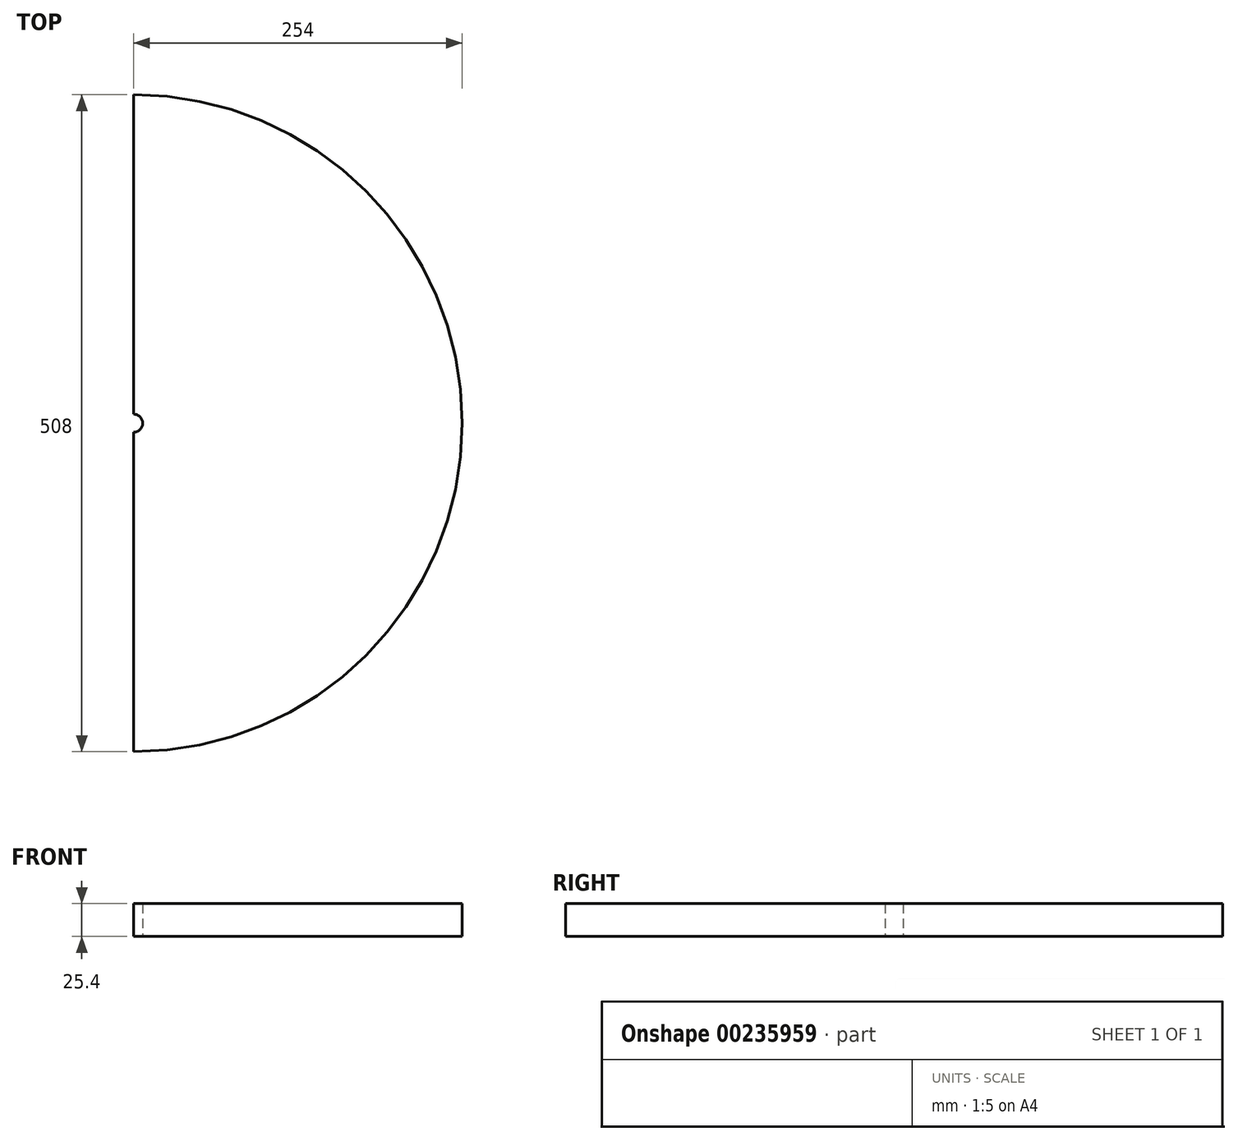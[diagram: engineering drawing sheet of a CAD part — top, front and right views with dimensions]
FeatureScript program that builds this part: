
annotation { "Feature Type Name" : "Feature", "Feature Type Description" : "" }
export const myFeature = defineFeature(function(context is Context, id is Id, definition is map)
    precondition{}
    {
        {
            var Q0;
            Q0=qCreatedBy(makeId("Top.planeOp"),FACE);
            var sketch = newSketch(context, id + "F0", { "sketchPlane" : qUnion([Q0])});
            skCircle(sketch, "E0", {"center": v(0, 0) * mm, "radius": 254 * mm});
            skCircle(sketch, "E1", {"center": v(0, 0) * mm, "radius": 6.99 * mm});
            skLineSegment(sketch, "E2", {"start": v(0, 0) * mm, "end": v(0, 254) * mm});
            skLineSegment(sketch, "E3", {"start": v(0, 0) * mm, "end": v(0, -254) * mm});
            skSolve(sketch);
        }
        {
            var Q0;
            {var subQ0=sQuery(id+"F0.wireOp",EDGE,"E2");var subQ1=sQuery(id+"F0.wireOp",EDGE,"E0");var subQ2=makeQuery(id+"F0.imprint","INTERSECT",VERTEX,{"derivedFrom":[subQ1,subQ0]});Q0=makeQuery(id+"F0.imprint","IMPRINT",FACE,{"disambiguationData":[TD([[makeQuery(id+"F0.imprint","IMPRINT",EDGE,{"disambiguationData":[TD([[subQ2,1.0]])],"derivedFrom":subQ1}),1.0]])]});}
            extrude(context, id + "F1", {"entities" : qUnion([Q0]), "depth" : 25.4 * mm});
        }
    });
